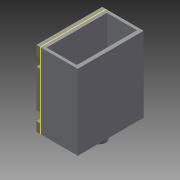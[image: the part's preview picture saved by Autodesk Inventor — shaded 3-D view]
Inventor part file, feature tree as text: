
AUTODESK INVENTOR PART (.ipt)
format: ipt  version: 2014 SP2 (Build 180246200, 246)  size: 119,296 bytes
history: native  units: mm
features: sketch x7, extrude x5
ambient origin geometry x8: Origin, YZ Plane, XZ Plane, XY Plane, X Axis, Y Axis, Z Axis, Center Point
bodies: Solid1 (feature_tree)
feature tree (12):
  extrude  "Extrusion1"  Depth=35.0mm
  extrude  "Extrusion2"  Depth=16.0mm
  sketch  "Sketch3"  dims[d5=32.0mm d6=30.0mm d7=0.0mm]
  sketch  "Sketch5"  dims[d16=5.0mm d17=5.0mm]
  extrude  "Extrusion3"  Depth=30.0mm TaperAngle=0.0deg
  extrude  "Extrusion4"  Depth=5.0mm
  extrude  "Extrusion5"  Depth=2.0mm TaperAngle=0.0deg
  sketch  "Sketch1"  dims[d0=20.0mm d1=35.0mm]
  sketch  "Sketch2"  dims[d2=40.0mm d3=0.0mm d4=16.0mm]
  sketch  "Sketch6"  dims[d18=20.0mm d19=2.0mm d20=0.0mm]
  sketch  "Sketch7"  dims[d21=4.5mm]
  sketch  "Sketch8"  dims[d22=4.0mm d23=0.0mm d24=7.0mm d25=8.0mm d26=0.0mm]
